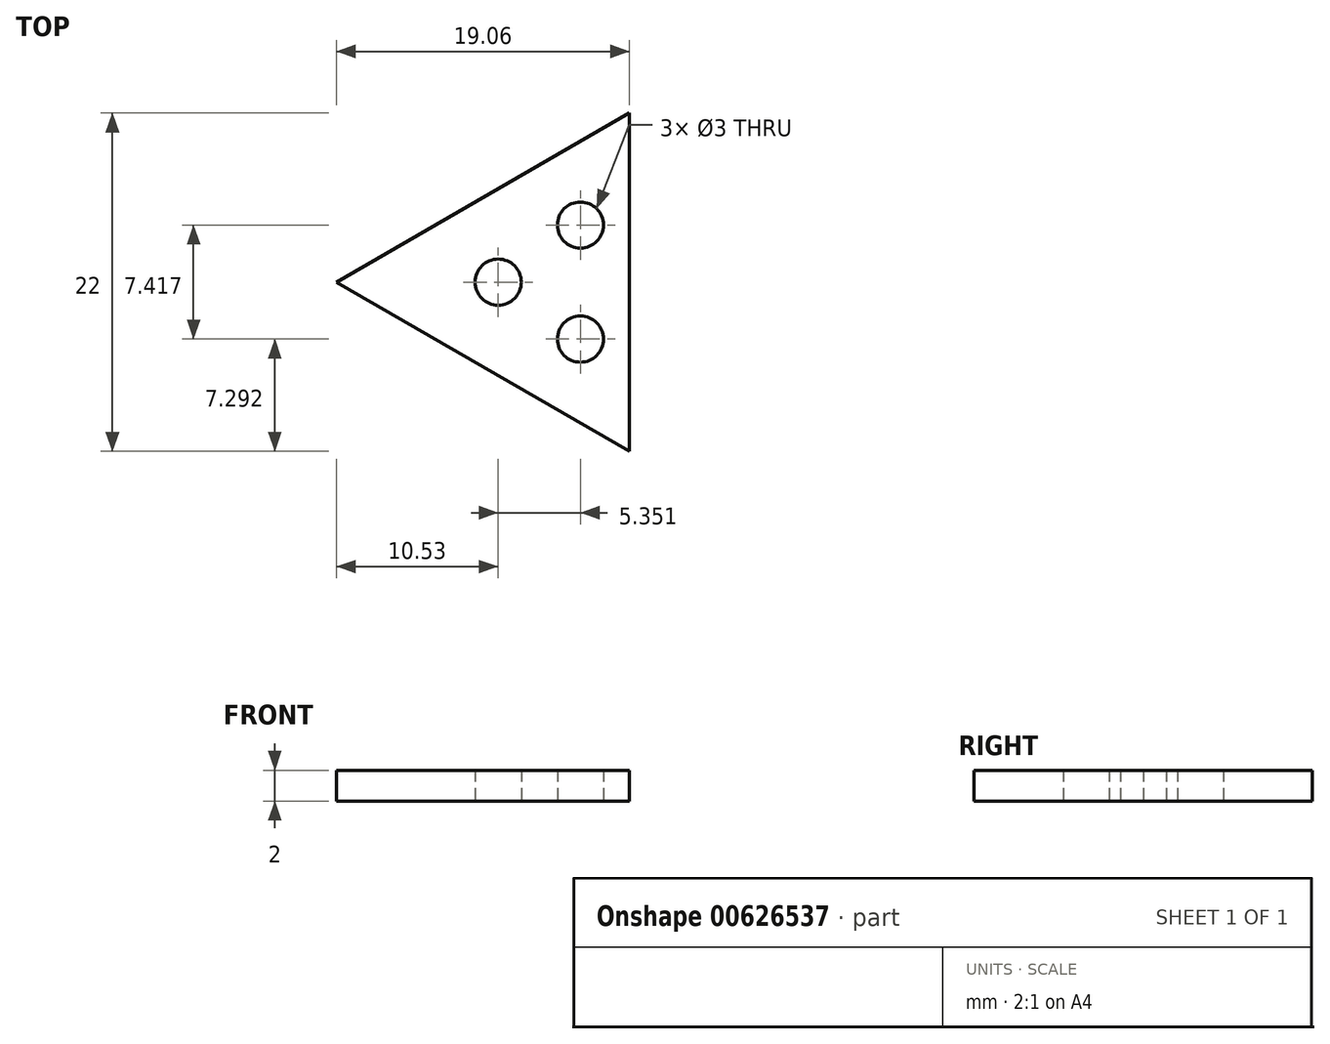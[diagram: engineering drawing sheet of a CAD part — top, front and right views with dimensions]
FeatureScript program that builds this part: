
annotation { "Feature Type Name" : "Feature", "Feature Type Description" : "" }
export const myFeature = defineFeature(function(context is Context, id is Id, definition is map)
    precondition{}
    {
        {
            var Q0;
            Q0=qCreatedBy(makeId("Top.planeOp"),FACE);
            var sketch = newSketch(context, id + "F0", { "sketchPlane" : qUnion([Q0])});
            skLineSegment(sketch, "E0.1.0", {"start": v(-9.53, 0) * mm, "end": v(9.53, -11) * mm});
            skLineSegment(sketch, "E0.1.2", {"start": v(9.53, -11) * mm, "end": v(9.53, 11) * mm});
            skLineSegment(sketch, "E1", {"start": v(-9.53, 0) * mm, "end": v(9.53, 11) * mm});
            skLineSegment(sketch, "E2", {"start": v(9.53, 0) * mm, "end": v(-9.53, 0) * mm, "construction": true});
            skLineSegment(sketch, "E3", {"start": v(0, -5.5) * mm, "end": v(0, 5.5) * mm, "construction": true});
            skPoint(sketch, "E4", {"position": v(9.8, -10) * mm});
            skPoint(sketch, "E5.MirrorP", {"position": v(9.8, 10) * mm});
            skPoint(sketch, "E6", {"position": v(-7.53, 0) * mm});
            skLineSegment(sketch, "E7", {"start": v(9.53, -10) * mm, "end": v(9.53, 10) * mm});
            skLineSegment(sketch, "E8", {"start": v(8.8, 1.88) * mm, "end": v(9.53, 1.88) * mm, "construction": true});
            skLineSegment(sketch, "E9", {"start": v(1.2, 5.61) * mm, "end": v(0.94, 6.04) * mm, "construction": true});
            skPoint(sketch, "E10", {"position": v(-8.53, 0) * mm});
            skLineSegment(sketch, "E11", {"start": v(-1.66, 4.54) * mm, "end": v(-1.23, 3.79) * mm, "construction": true});
            skLineSegment(sketch, "E12", {"start": v(-2.22, -4.22) * mm, "end": v(-1.79, -3.47) * mm, "construction": true});
            skCircle(sketch, "E13.4.0", {"center": v(6.35, -3.7) * mm, "radius": 1.5 * mm});
            skCircle(sketch, "E13.4.1", {"center": v(1, 0) * mm, "radius": 1.5 * mm});
            skCircle(sketch, "E13.4.2", {"center": v(6.35, 3.7) * mm, "radius": 1.5 * mm});
            skPoint(sketch, "E13.center", {"position": v(-1.54, -22.87) * mm});
            skLineSegment(sketch, "E14", {"start": v(0, 0) * mm, "end": v(1, 0) * mm, "construction": true});
            skSolve(sketch);
        }
        {
            var Q0;
            Q0 = qSketchRegion(id + "F0", true);
            extrude(context, id + "F1", {"entities" : qUnion([Q0]), "depth" : 2 * mm, "offsetDistance" : 25 * mm});
        }
    });
